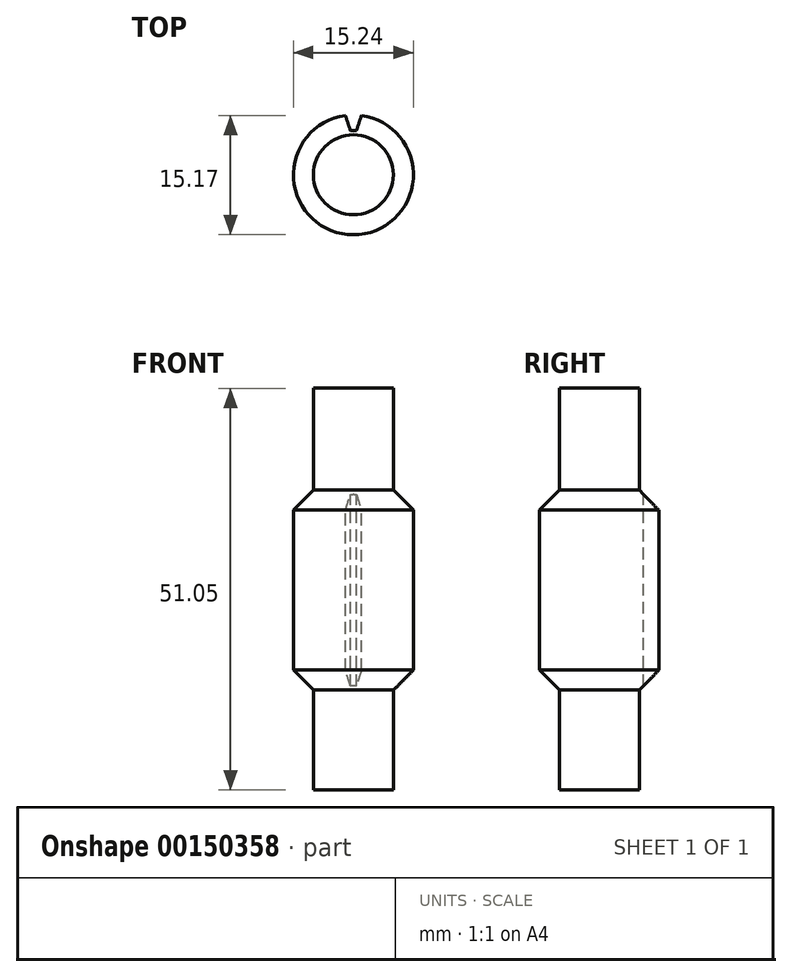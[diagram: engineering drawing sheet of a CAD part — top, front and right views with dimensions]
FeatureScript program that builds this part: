
annotation { "Feature Type Name" : "Feature", "Feature Type Description" : "" }
export const myFeature = defineFeature(function(context is Context, id is Id, definition is map)
    precondition{}
    {
        {
            var Q0;
            Q0=qCreatedBy(makeId("Top.planeOp"),FACE);
            var sketch = newSketch(context, id + "F0", { "sketchPlane" : qUnion([Q0])});
            skCircle(sketch, "E0", {"center": v(0, 0) * mm, "radius": 7.62 * mm});
            skSolve(sketch);
        }
        {
            var Q0;
            Q0 = qSketchRegion(id + "F0", true);
            extrude(context, id + "F1", {"entities" : qUnion([Q0]), "depth" : 25.4 * mm});
        }
        {
            var Q0;
            Q0=makeQuery(id+"F1.opExtrude","CAP_EDGE",EDGE,{"disambiguationData":[OSD([sQuery(id+"F0.wireOp",EDGE,"E0")])],"isStart":false});
            var Q1;
            Q1=makeQuery(id+"F1.opExtrude","CAP_EDGE",EDGE,{"disambiguationData":[OSD([sQuery(id+"F0.wireOp",EDGE,"E0")])],"isStart":true});
            chamfer(context, id + "F2", {"entities" : qUnion([Q0, Q1]), "width" : 2.54 * mm, "tangentPropagation" : true});
        }
        {
            var Q0;
            Q0=makeQuery(id+"F1.opExtrude","CAP_FACE",FACE,{"disambiguationData":[OSD([sQuery(id+"F0.wireOp",EDGE,"E0")])],"isStart":false});
            var sketch = newSketch(context, id + "F3", { "sketchPlane" : qUnion([Q0])});
            skLineSegment(sketch, "E1", {"start": v(-1.02, 7.55) * mm, "end": v(-0.38, 5.59) * mm});
            skLineSegment(sketch, "E2", {"start": v(-0.38, 5.59) * mm, "end": v(0.38, 5.59) * mm});
            skLineSegment(sketch, "E3", {"start": v(0.38, 5.59) * mm, "end": v(1.02, 7.55) * mm});
            skArc(sketch, "E4", {"start": v(1.02, 7.55) * mm, "mid": v(0, 7.62) * mm, "end": v(-1.02, 7.55) * mm});
            skPoint(sketch, "E5", {"position": v(0, 5.59) * mm});
            skPoint(sketch, "E6", {"position": v(0, 7.62) * mm});
            skSolve(sketch);
        }
        {
            var Q0;
            Q0 = qSketchRegion(id + "F3", true);
            var Q1;
            Q1=makeQuery(id+"F1.opExtrude","CAP_FACE",FACE,{"disambiguationData":[OSD([sQuery(id+"F0.wireOp",EDGE,"E0")])],"isStart":true});
            extrude(context, id + "F4", {"entities" : qUnion([Q0]), "operationType" : NewBodyOperationType.REMOVE, "endBound" : BoundingType.UP_TO_SURFACE, "oppositeDirection" : true, "endBoundEntityFace" : qUnion([Q1]), "depth" : 25.4 * mm});
        }
        {
            var Q0;
            Q0=qCreatedBy(makeId("Front.planeOp"),FACE);
            var sketch = newSketch(context, id + "F5", { "sketchPlane" : qUnion([Q0])});
            skLineSegment(sketch, "E7", {"start": v(0, 0) * mm, "end": v(0, 6.35) * mm, "construction": true});
            skSolve(sketch);
        }
        {
            var Q0;
            Q0=makeQuery(id+"F1.opExtrude","CAP_FACE",FACE,{"disambiguationData":[OSD([sQuery(id+"F0.wireOp",EDGE,"E0")])],"isStart":false});
            var sketch = newSketch(context, id + "F6", { "sketchPlane" : qUnion([Q0])});
            skCircle(sketch, "E8", {"center": v(0, 0) * mm, "radius": 5.08 * mm});
            skSolve(sketch);
        }
        {
            var Q0;
            Q0 = qSketchRegion(id + "F6", true);
            extrude(context, id + "F7", {"entities" : qUnion([Q0]), "operationType" : NewBodyOperationType.ADD, "depth" : 12.95 * mm});
        }
        {
            var Q0;
            Q0=makeQuery(id+"F1.opExtrude","CAP_FACE",FACE,{"disambiguationData":[OSD([sQuery(id+"F0.wireOp",EDGE,"E0")])],"isStart":true});
            var sketch = newSketch(context, id + "F8", { "sketchPlane" : qUnion([Q0])});
            skCircle(sketch, "E9", {"center": v(0, 0) * mm, "radius": 5.08 * mm});
            skSolve(sketch);
        }
        {
            var Q0;
            Q0 = qSketchRegion(id + "F8", true);
            extrude(context, id + "F9", {"entities" : qUnion([Q0]), "operationType" : NewBodyOperationType.ADD, "depth" : 12.7 * mm});
        }
    });
